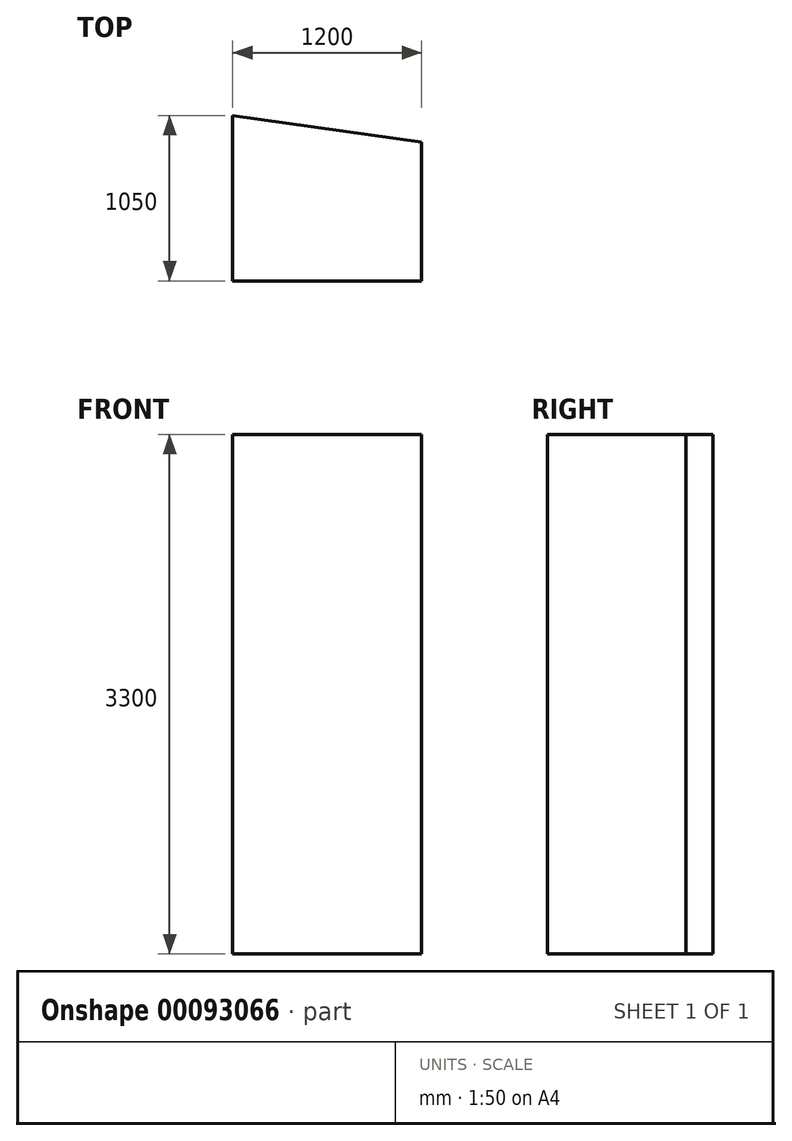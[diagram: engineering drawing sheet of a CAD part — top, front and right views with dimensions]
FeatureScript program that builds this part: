
annotation { "Feature Type Name" : "Feature", "Feature Type Description" : "" }
export const myFeature = defineFeature(function(context is Context, id is Id, definition is map)
    precondition{}
    {
        {
            var Q0;
            Q0=qCreatedBy(makeId("Top.planeOp"),FACE);
            var sketch = newSketch(context, id + "F0", { "sketchPlane" : qUnion([Q0])});
            skLineSegment(sketch, "E0", {"start": v(1200.16, 880.06) * mm, "end": v(1200.16, 0.06) * mm});
            skLineSegment(sketch, "E1.0", {"start": v(0.16, 1050.06) * mm, "end": v(0.16, 0.06) * mm});
            skLineSegment(sketch, "E2", {"start": v(0.16, 0.06) * mm, "end": v(1200.16, 0.06) * mm});
            skLineSegment(sketch, "E3", {"start": v(0.16, 1050.06) * mm, "end": v(1200.16, 880.06) * mm});
            skSolve(sketch);
        }
        {
            var Q0;
            Q0 = qSketchRegion(id + "F0", true);
            extrude(context, id + "F1", {"entities" : qUnion([Q0]), "depth" : 3300 * mm});
        }
    });
